# Revit family: DCS_Revit_18_BC-BOTTLEAC-25_Bottle_Holder_9000079A
name_source: partatom
category: Specialty Equipment
revit_build: Autodesk Revit 2018 (Build: 20170223_1515(x64)
units: mm (PartAtom-declared; Revit-internal decimal feet)

## family parameters
Always vertical = Yes
Cut with Voids When Loaded = Yes
OmniClass Number = 23.40.40.14.24.11
OmniClass Title = Bar Equipment
Part Type = Normal
Room Calculation Point = No
Round Connector Dimension = Use Diameter
Shared = No
Work Plane-Based = No

## types (3) — shared parameters
Cavity - Depth = 535 mm  [stored 1.75525 ft]
Cavity - Height = 250 mm  [stored 0.82021 ft]
Cavity - Width = 615 mm  [stored 2.01772 ft]
Description = Series 7, Beverage Chiller Bottle Holder Accessory
Manufacturer = Fisher & Paykel
Material - Body = DCS - Stainless Steel
Model = BC-BOTTLEAC-25
Product - Depth = 710 mm
Product - Height = 306 mm  [stored 1.00394 ft]
Product - Width = 670 mm  [stored 2.19816 ft]
URL = www.dcsappliances.com
Visibility - Clearance Required = Yes

## per-type parameters (varying)
| type | Connector Description - Sanitary | Visibility - BC25 Beverage Chiller | Visibility - Cover |
| Bottle Holder |  | No | No |
| Bottle Holder with BC25 Beverage Chiller (without cover) | 1-1/2” NPS male thread | Yes | No |
| Bottle Holder with BC25 Beverage Chiller |  | Yes | Yes |

note: [stored X ft] marks values corroborated as IEEE doubles in the binary element streams (Revit-internal decimal feet)

## geometry (parser evidence)
native form markers: Sweep x5
no freeform markers — native parametric forms only
